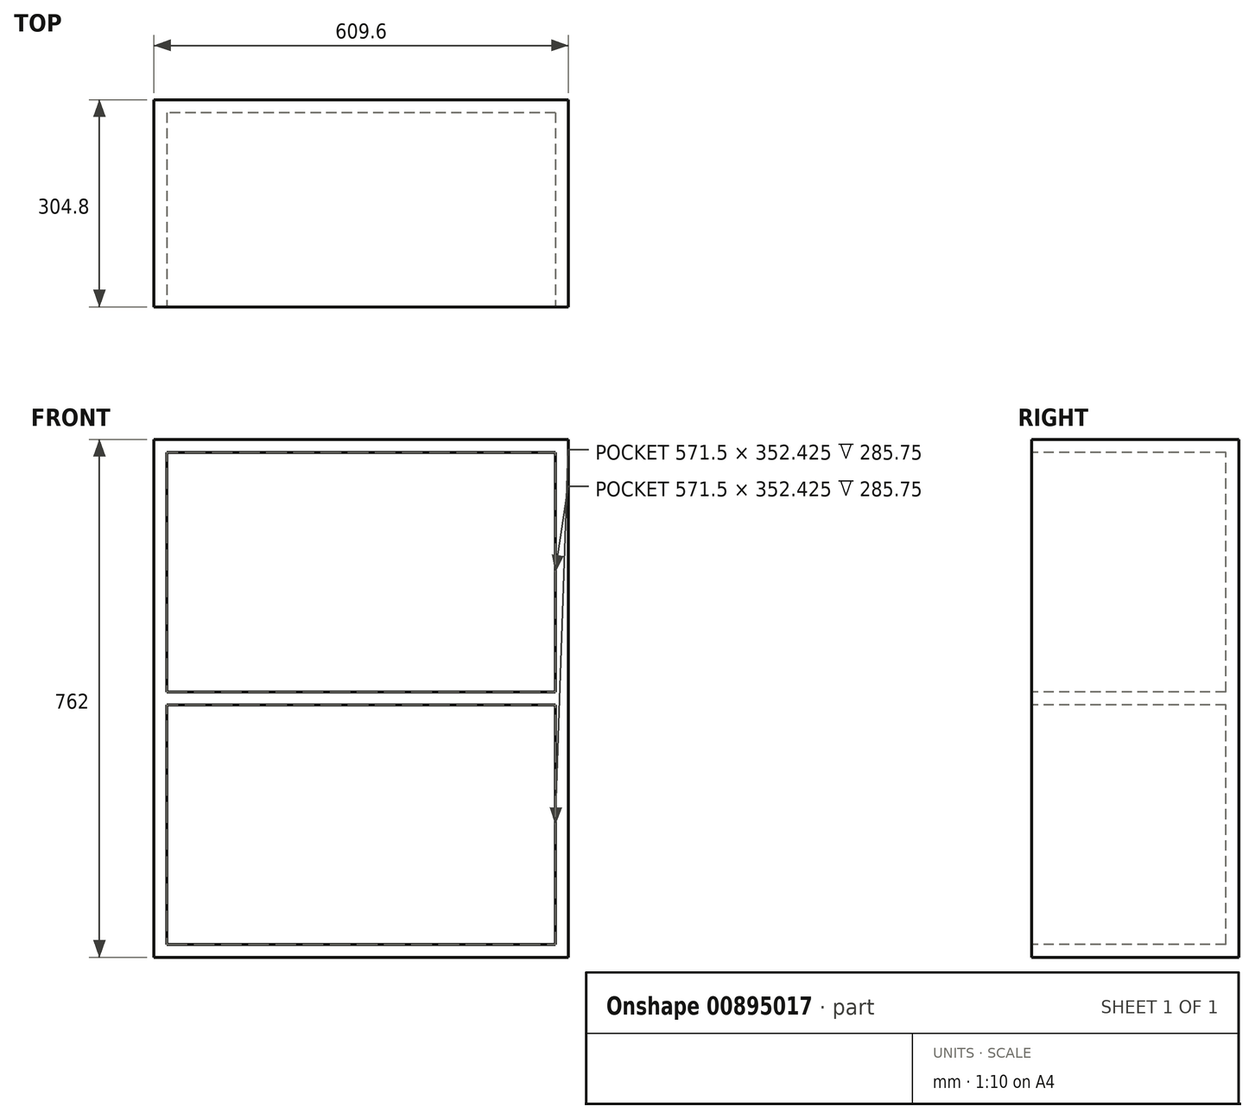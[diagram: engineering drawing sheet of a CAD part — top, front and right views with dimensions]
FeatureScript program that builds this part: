
annotation { "Feature Type Name" : "Feature", "Feature Type Description" : "" }
export const myFeature = defineFeature(function(context is Context, id is Id, definition is map)
    precondition{}
    {
        {
            var Q0;
            Q0=qCreatedBy(makeId("Front.planeOp"),FACE);
            var sketch = newSketch(context, id + "F0", { "sketchPlane" : qUnion([Q0])});
            skLineSegment(sketch, "E0.bottom", {"start": v(304.8, 381) * mm, "end": v(-304.8, 381) * mm});
            skLineSegment(sketch, "E0.top", {"start": v(304.8, -381) * mm, "end": v(-304.8, -381) * mm});
            skLineSegment(sketch, "E0.left", {"start": v(304.8, 381) * mm, "end": v(304.8, -381) * mm});
            skLineSegment(sketch, "E0.right", {"start": v(-304.8, 381) * mm, "end": v(-304.8, -381) * mm});
            skPoint(sketch, "E0.middle", {"position": v(0, 0) * mm});
            skSolve(sketch);
        }
        {
            var Q0;
            Q0=makeQuery(id+"F0.imprint","IMPRINT",FACE,{"disambiguationData":[TD([[makeQuery(id+"F0.imprint","IMPRINT",EDGE,{"derivedFrom":sQuery(id+"F0.wireOp",EDGE,"E0.bottom")}),1.0]])]});
            extrude(context, id + "F1", {"entities" : qUnion([Q0]), "depth" : 304.8 * mm, "offsetDistance" : 25.4 * mm});
        }
        {
            var Q0;
            Q0=makeQuery(id+"F1.opExtrude","CAP_FACE",FACE,{"disambiguationData":[OSD([sQuery(id+"F0.wireOp",EDGE,"E0.bottom"),sQuery(id+"F0.wireOp",EDGE,"E0.top"),sQuery(id+"F0.wireOp",EDGE,"E0.left"),sQuery(id+"F0.wireOp",EDGE,"E0.right")])],"isStart":false});
            var sketch = newSketch(context, id + "F2", { "sketchPlane" : qUnion([Q0])});
            skLineSegment(sketch, "E1.bottom", {"start": v(-285.75, 361.95) * mm, "end": v(285.75, 361.95) * mm});
            skLineSegment(sketch, "E1.top", {"start": v(-285.75, 9.52) * mm, "end": v(285.75, 9.53) * mm});
            skLineSegment(sketch, "E1.left", {"start": v(-285.75, 361.95) * mm, "end": v(-285.75, 9.53) * mm});
            skLineSegment(sketch, "E1.right", {"start": v(285.75, 361.95) * mm, "end": v(285.75, 9.53) * mm});
            skLineSegment(sketch, "E2.bottom", {"start": v(-285.75, -9.53) * mm, "end": v(285.75, -9.52) * mm});
            skLineSegment(sketch, "E2.top", {"start": v(-285.75, -361.95) * mm, "end": v(285.75, -361.95) * mm});
            skLineSegment(sketch, "E2.left", {"start": v(-285.75, -9.53) * mm, "end": v(-285.75, -361.95) * mm});
            skLineSegment(sketch, "E2.right", {"start": v(285.75, -9.52) * mm, "end": v(285.75, -361.95) * mm});
            skSolve(sketch);
        }
        {
            var Q0;
            Q0=makeQuery(id+"F2.imprint","IMPRINT",FACE,{"disambiguationData":[TD([[makeQuery(id+"F2.imprint","IMPRINT",EDGE,{"derivedFrom":sQuery(id+"F2.wireOp",EDGE,"E1.bottom")}),-1.0]])]});
            var Q1;
            Q1=makeQuery(id+"F2.imprint","IMPRINT",FACE,{"disambiguationData":[TD([[makeQuery(id+"F2.imprint","IMPRINT",EDGE,{"derivedFrom":sQuery(id+"F2.wireOp",EDGE,"E2.bottom")}),-1.0]])]});
            var Q2;
            Q2=makeQuery(id+"F1.opExtrude","CAP_FACE",FACE,{"disambiguationData":[OSD([sQuery(id+"F0.wireOp",EDGE,"E0.bottom"),sQuery(id+"F0.wireOp",EDGE,"E0.top"),sQuery(id+"F0.wireOp",EDGE,"E0.left"),sQuery(id+"F0.wireOp",EDGE,"E0.right")])],"isStart":true});
            extrude(context, id + "F3", {"entities" : qUnion([Q0, Q1]), "operationType" : NewBodyOperationType.REMOVE, "endBound" : BoundingType.UP_TO_SURFACE, "oppositeDirection" : true, "depth" : 25.4 * mm, "endBoundEntityFace" : qUnion([Q2]), "hasOffset" : true, "offsetDistance" : 19.05 * mm});
        }
    });
